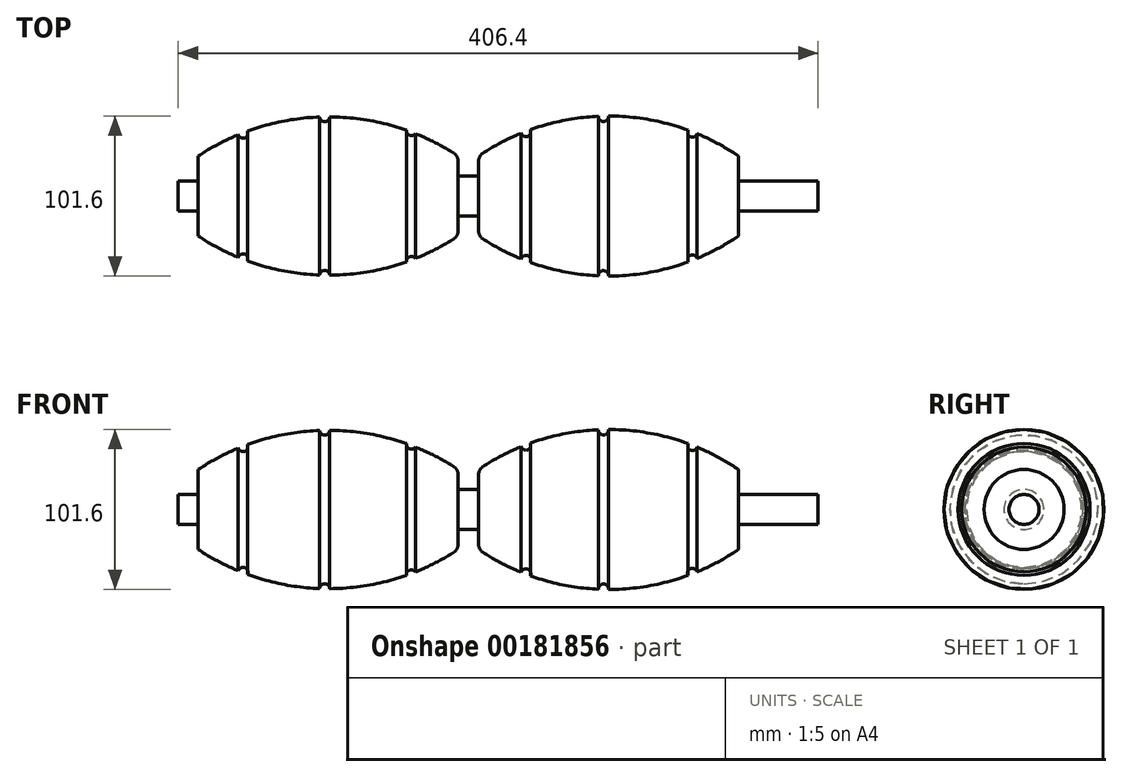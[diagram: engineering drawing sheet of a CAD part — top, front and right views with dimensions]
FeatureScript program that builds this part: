
annotation { "Feature Type Name" : "Feature", "Feature Type Description" : "" }
export const myFeature = defineFeature(function(context is Context, id is Id, definition is map)
    precondition{}
    {
        {
            var Q0;
            Q0=qCreatedBy(makeId("Right.planeOp"),FACE);
            var sketch = newSketch(context, id + "F0", { "sketchPlane" : qUnion([Q0])});
            skCircle(sketch, "E0", {"center": v(0, 0) * mm, "radius": 9.53 * mm});
            skSolve(sketch);
        }
        {
            var Q0;
            Q0=makeQuery(id+"F0.imprint","IMPRINT",FACE,{"disambiguationData":[TD([[makeQuery(id+"F0.imprint","IMPRINT",EDGE,{"derivedFrom":sQuery(id+"F0.wireOp",EDGE,"E0")}),1.0]])]});
            extrude(context, id + "F1", {"entities" : qUnion([Q0]), "depth" : 406.4 * mm});
        }
        {
            var Q0;
            Q0=qCreatedBy(makeId("Front.planeOp"),FACE);
            var sketch = newSketch(context, id + "F2", { "sketchPlane" : qUnion([Q0])});
            skLineSegment(sketch, "E1", {"start": v(12.7, 12.7) * mm, "end": v(12.7, 25.4) * mm});
            skLineSegment(sketch, "E2", {"start": v(177.8, 21.95) * mm, "end": v(177.8, 12.7) * mm});
            skLineSegment(sketch, "E3", {"start": v(177.8, 12.7) * mm, "end": v(190.75, 12.7) * mm});
            skLineSegment(sketch, "E4", {"start": v(190.75, 12.7) * mm, "end": v(190.75, 22) * mm});
            skLineSegment(sketch, "E5", {"start": v(190.75, 25.4) * mm, "end": v(191.75, 25.4) * mm});
            skLineSegment(sketch, "E6", {"start": v(355.85, 25.4) * mm, "end": v(355.85, 12.7) * mm});
            skArc(sketch, "E7", {"start": v(174.84, 27.32) * mm, "mid": v(93.48, 50.3) * mm, "end": v(12.7, 25.4) * mm});
            skArc(sketch, "E8", {"start": v(355.85, 25.4) * mm, "mid": v(275.05, 50.79) * mm, "end": v(193.66, 27.33) * mm});
            skPoint(sketch, "E9.visualSharp", {"position": v(177.8, 25.4) * mm});
            skArc(sketch, "E9.filletArc", {"start": v(177.8, 21.95) * mm, "mid": v(177, 25.01) * mm, "end": v(174.84, 27.32) * mm});
            skPoint(sketch, "E10.visualSharp", {"position": v(190.75, 25.4) * mm});
            skArc(sketch, "E10.filletArc", {"start": v(193.66, 27.33) * mm, "mid": v(191.53, 25.03) * mm, "end": v(190.75, 22) * mm});
            skLineSegment(sketch, "E11", {"start": v(190.75, 12.7) * mm, "end": v(177.8, 12.7) * mm});
            skPoint(sketch, "E12.orphan", {"position": v(355.85, 0) * mm});
            skPoint(sketch, "E13.end.orphan", {"position": v(12.7, 0) * mm});
            skPoint(sketch, "E14.end.orphan", {"position": v(22.06, 12.7) * mm});
            skLineSegment(sketch, "E15", {"start": v(12.7, 12.7) * mm, "end": v(12.7, 0) * mm});
            skLineSegment(sketch, "E16", {"start": v(355.85, 12.7) * mm, "end": v(355.85, 0) * mm});
            skLineSegment(sketch, "E17", {"start": v(12.7, 0) * mm, "end": v(0, 0) * mm});
            skLineSegment(sketch, "E18", {"start": v(355.85, 0) * mm, "end": v(12.7, 0) * mm});
            skSolve(sketch);
        }
        {
            var Q0;
            Q0 = qSketchRegion(id + "F2", true);
            var Q1;
            Q1=makeQuery(id+"F1.opExtrude","SWEPT_FACE",FACE,{"disambiguationData":[OSD([sQuery(id+"F0.wireOp",EDGE,"E0")])]});
            revolve(context, id + "F3", {"operationType" : NewBodyOperationType.ADD, "entities" : qUnion([Q0]), "axis" : qUnion([Q1]), "revolveType" : RevolveType.FULL});
        }
        {
            var Q0;
            Q0=qCreatedBy(makeId("Front.planeOp"),FACE);
            var sketch = newSketch(context, id + "F4", { "sketchPlane" : qUnion([Q0])});
            skCircle(sketch, "E19", {"center": v(92.95, 50.39) * mm, "radius": 3.18 * mm});
            skCircle(sketch, "E20", {"center": v(41.18, 39.9) * mm, "radius": 3.18 * mm});
            skCircle(sketch, "E21", {"center": v(148.1, 41.48) * mm, "radius": 3.18 * mm});
            skCircle(sketch, "E22", {"center": v(270.07, 50.51) * mm, "radius": 3.18 * mm});
            skCircle(sketch, "E23", {"center": v(220.85, 40.82) * mm, "radius": 3.18 * mm});
            skCircle(sketch, "E24", {"center": v(326.49, 40.57) * mm, "radius": 3.18 * mm});
            skSolve(sketch);
        }
        {
            var Q0;
            Q0 = qSketchRegion(id + "F4", true);
            var Q1;
            Q1=makeQuery(id+"F3.opRevolve","SWEPT_FACE",FACE,{"disambiguationData":[OSD([sQuery(id+"F2.wireOp",EDGE,"E7")])]});
            revolve(context, id + "F5", {"operationType" : NewBodyOperationType.REMOVE, "entities" : qUnion([Q0]), "axis" : qUnion([Q1]), "revolveType" : RevolveType.FULL, "oppositeDirection" : true});
        }
    });
